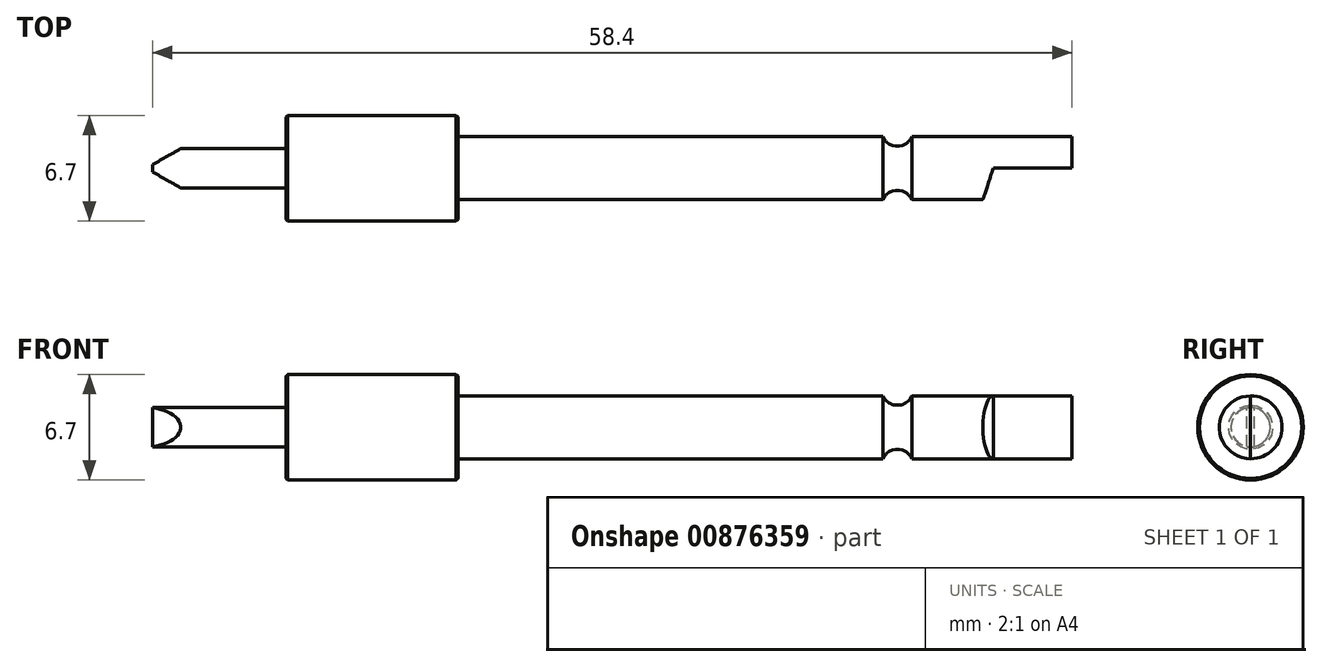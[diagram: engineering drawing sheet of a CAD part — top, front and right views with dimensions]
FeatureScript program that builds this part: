
annotation { "Feature Type Name" : "Feature", "Feature Type Description" : "" }
export const myFeature = defineFeature(function(context is Context, id is Id, definition is map)
    precondition{}
    {
        {
            var Q0;
            Q0=qCreatedBy(makeId("Front.planeOp"),FACE);
            var sketch = newSketch(context, id + "F0", { "sketchPlane" : qUnion([Q0])});
            skLineSegment(sketch, "E0", {"start": v(-32.5, 0) * mm, "end": v(32.5, 0) * mm, "construction": true});
            skLineSegment(sketch, "E1", {"start": v(-30, 0) * mm, "end": v(-30, 1.25) * mm});
            skLineSegment(sketch, "E2", {"start": v(-30, 1.25) * mm, "end": v(-21.5, 1.25) * mm});
            skLineSegment(sketch, "E3", {"start": v(-21.5, 1.25) * mm, "end": v(-21.5, 3.35) * mm});
            skLineSegment(sketch, "E4", {"start": v(-21.5, 3.35) * mm, "end": v(-10.6, 3.35) * mm});
            skLineSegment(sketch, "E5", {"start": v(-10.6, 3.35) * mm, "end": v(-10.6, 2) * mm});
            skLineSegment(sketch, "E6", {"start": v(-10.6, 2) * mm, "end": v(16.4, 2) * mm});
            skArc(sketch, "E7", {"start": v(16.4, 2) * mm, "mid": v(17.32, 1.4) * mm, "end": v(18.23, 2) * mm});
            skLineSegment(sketch, "E8", {"start": v(18.23, 2) * mm, "end": v(28.4, 2) * mm});
            skLineSegment(sketch, "E9", {"start": v(28.4, 0) * mm, "end": v(-30, 0) * mm});
            skLineSegment(sketch, "E10", {"start": v(28.4, 2) * mm, "end": v(28.4, 0) * mm});
            skSolve(sketch);
        }
        {
            var Q0;
            Q0 = qSketchRegion(id + "F0", true);
            var Q1;
            Q1=sQuery(id+"F0.wireOp",EDGE,"E0");
            revolve(context, id + "F1", {"surfaceOperationType" : NewSurfaceOperationType.NEW, "entities" : qUnion([Q0]), "axis" : qUnion([Q1]), "revolveType" : RevolveType.FULL});
        }
        {
            var Q0;
            Q0=qCreatedBy(makeId("Top.planeOp"),FACE);
            var sketch = newSketch(context, id + "F2", { "sketchPlane" : qUnion([Q0])});
            skLineSegment(sketch, "E11", {"start": v(28.4, 0) * mm, "end": v(23.4, 0) * mm});
            skLineSegment(sketch, "E12", {"start": v(23.4, 0) * mm, "end": v(22.75, -2) * mm});
            skLineSegment(sketch, "E13", {"start": v(22.75, -2) * mm, "end": v(28.4, -2) * mm});
            skLineSegment(sketch, "E14", {"start": v(28.4, -2) * mm, "end": v(28.4, 0) * mm});
            skSolve(sketch);
        }
        {
            var Q0;
            Q0 = qSketchRegion(id + "F2", true);
            extrude(context, id + "F3", {"entities" : qUnion([Q0]), "operationType" : NewBodyOperationType.REMOVE, "endBound" : BoundingType.SYMMETRIC, "depth" : 25 * mm, "offsetDistance" : 25 * mm});
        }
        {
            var Q0;
            Q0=qCreatedBy(makeId("Top.planeOp"),FACE);
            var sketch = newSketch(context, id + "F4", { "sketchPlane" : qUnion([Q0])});
            skLineSegment(sketch, "E15", {"start": v(-30, -0.23) * mm, "end": v(-30, 0.23) * mm});
            skLineSegment(sketch, "E16", {"start": v(-30, 0.23) * mm, "end": v(-28.2, 1.25) * mm});
            skLineSegment(sketch, "E17", {"start": v(-28.2, -1.25) * mm, "end": v(-30, -0.23) * mm});
            skLineSegment(sketch, "E18", {"start": v(-30, 0.23) * mm, "end": v(-30, 1.25) * mm});
            skLineSegment(sketch, "E19", {"start": v(-30, 1.25) * mm, "end": v(-28.2, 1.25) * mm});
            skLineSegment(sketch, "E20", {"start": v(-30, -0.22) * mm, "end": v(-30, -1.25) * mm});
            skLineSegment(sketch, "E21", {"start": v(-30, -1.25) * mm, "end": v(-28.2, -1.25) * mm});
            skSolve(sketch);
        }
        {
            var Q0;
            Q0 = qSketchRegion(id + "F4", true);
            extrude(context, id + "F5", {"entities" : qUnion([Q0]), "operationType" : NewBodyOperationType.REMOVE, "endBound" : BoundingType.SYMMETRIC, "oppositeDirection" : true, "depth" : 25 * mm, "offsetDistance" : 25 * mm});
        }
        {
            var Q0;
            Q0=makeQuery(id+"F1.opRevolve","SWEPT_EDGE",EDGE,{"disambiguationData":[OSD([sQuery(id+"F0.wireOp",EDGE,"E4"),sQuery(id+"F0.wireOp",EDGE,"E5")])]});
            var Q1;
            Q1=makeQuery(id+"F1.opRevolve","SWEPT_EDGE",EDGE,{"disambiguationData":[OSD([sQuery(id+"F0.wireOp",EDGE,"E3"),sQuery(id+"F0.wireOp",EDGE,"E4")])]});
            chamfer(context, id + "F6", {"entities" : qUnion([Q0, Q1]), "width" : 0.1 * mm, "tangentPropagation" : true});
        }
    });
